# Revit family: 60e8e82a-04c9-4052-aa8a-17596fd3e44a
name_source: partatom
category: Двери
revit_build: Autodesk Revit 2017 (Build: 20170419_0315(x64)
units: mm (PartAtom-declared; Revit-internal decimal feet)

## family parameters
Всегда вертикально = Да
Заголовок OmniClass = Doors
Номер OmniClass = 23.30.10.00
Общий = Нет
Основа = Стена
При загрузке вырезать с полостями = Нет
Точка расчета площади = Нет

## types (1)
- 60e8e82a-04c9-4052-aa8a-17596fd3e44a
    00_СмещениеОтСтены = 0 мм
    00_ШиринаКоробки = 5 мм
    00_ШиринаМонтажногоЗазора = 10 мм
    a = 2025 мм
    b = 2180 мм
    c = 2200 мм
    Аналитическая конструкция = <Нет>
    Высота = 2100 мм
    Выступ каркаса внут. = 25 мм
    Выступ каркаса нар. = 25 мм
    ДопРазмер = 205 мм
    Замыкание стены = По основе
    МатериалДверногоПолотна = <По категории>
    МатериалКоробки = <По категории>
    МатериалОстекления = Стекло
    МатериалПривода = <По категории>
    МатериалРучки = <По категории>
    МатерилаМонтажногоЗазора = <По категории>
    О_Масса = 0
    Примерная высота = 2100 мм
    Примерная ширина = 2000 мм
    Р_Высота = 2100 мм
    Р_Ширина = 2000 мм
    Функция = Внутренние слои
    Ширина = 2000 мм
    Ширина каркаса = 75 мм
